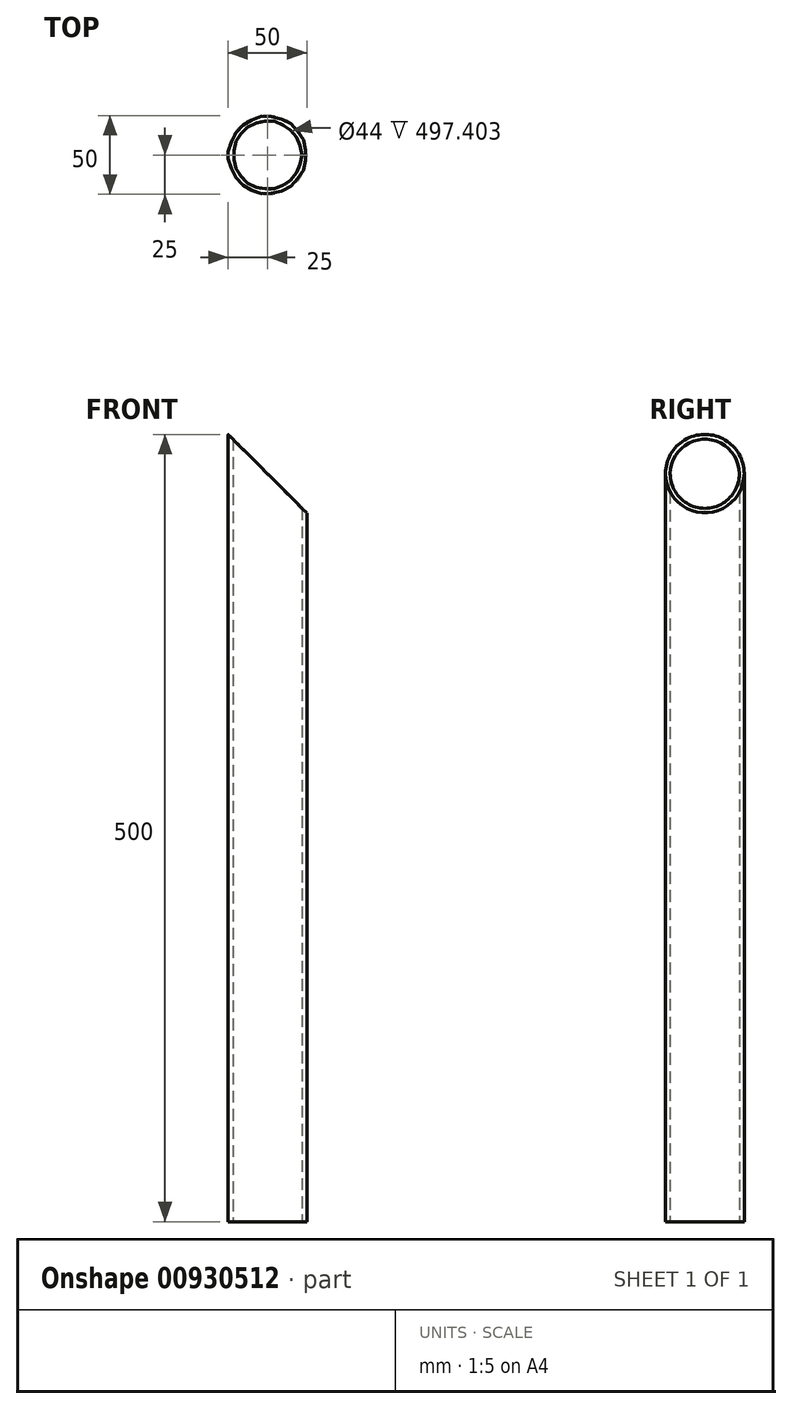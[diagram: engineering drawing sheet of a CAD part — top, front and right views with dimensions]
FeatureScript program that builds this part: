
annotation { "Feature Type Name" : "Feature", "Feature Type Description" : "" }
export const myFeature = defineFeature(function(context is Context, id is Id, definition is map)
    precondition{}
    {
        {
            var Q0;
            Q0=qCreatedBy(makeId("Top.planeOp"),FACE);
            var sketch = newSketch(context, id + "F0", { "sketchPlane" : qUnion([Q0])});
            skCircle(sketch, "E0", {"center": v(0, 0) * mm, "radius": 25 * mm});
            skCircle(sketch, "E1", {"center": v(0, 0) * mm, "radius": 22 * mm});
            skSolve(sketch);
        }
        {
            var Q0;
            Q0=qSketchRegion(id+"F0",true);
            extrude(context, id + "F1", {"entities" : qUnion([Q0]), "depth" : 500 * mm, "offsetDistance" : 25 * mm});
        }
        {
            var Q0;
            Q0=qCreatedBy(makeId("Front.planeOp"),FACE);
            var sketch = newSketch(context, id + "F2", { "sketchPlane" : qUnion([Q0])});
            skLineSegment(sketch, "E2", {"start": v(-24.95, 500.05) * mm, "end": v(25.05, 450.05) * mm});
            skLineSegment(sketch, "E3", {"start": v(25.05, 450.05) * mm, "end": v(25.05, 500.05) * mm});
            skLineSegment(sketch, "E4", {"start": v(25.05, 500.05) * mm, "end": v(-24.95, 500.05) * mm});
            skSolve(sketch);
        }
        {
            var Q0;
            Q0 = qSketchRegion(id + "F2", true);
            extrude(context, id + "F3", {"entities" : qUnion([Q0]), "operationType" : NewBodyOperationType.REMOVE, "endBound" : BoundingType.SYMMETRIC, "depth" : 80 * mm, "offsetDistance" : 25 * mm});
        }
    });
